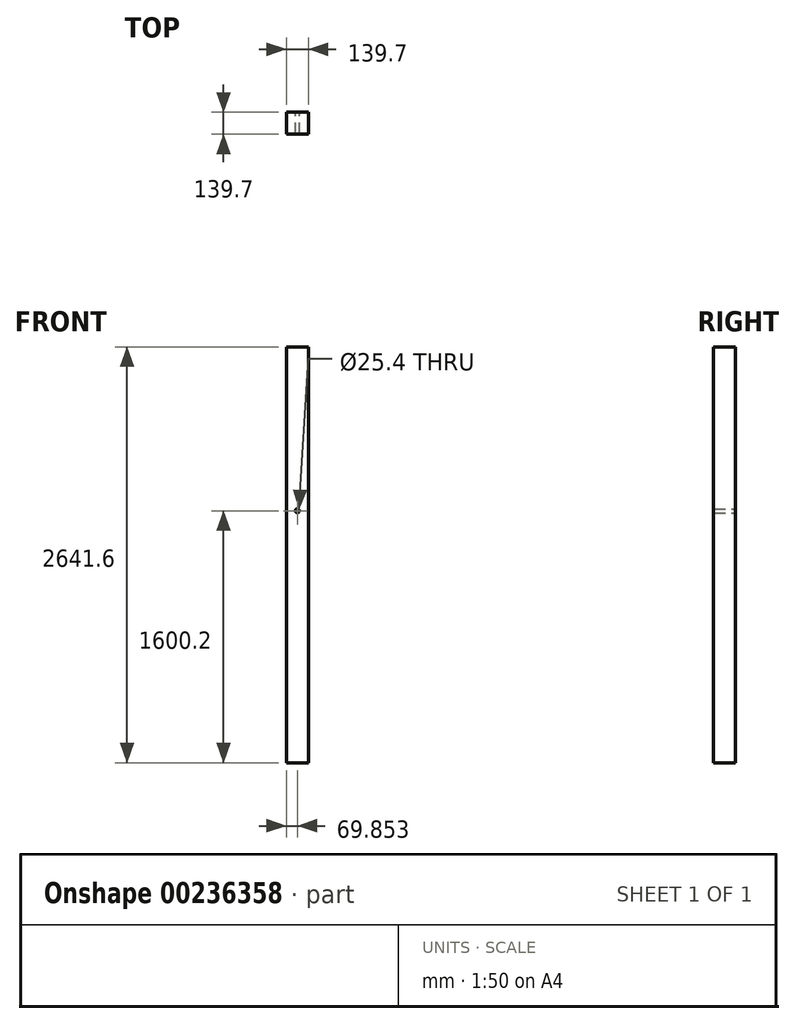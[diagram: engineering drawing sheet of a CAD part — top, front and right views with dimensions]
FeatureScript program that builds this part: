
annotation { "Feature Type Name" : "Feature", "Feature Type Description" : "" }
export const myFeature = defineFeature(function(context is Context, id is Id, definition is map)
    precondition{}
    {
        {
            var Q0;
            Q0=qCreatedBy(makeId("Front.planeOp"),FACE);
            var sketch = newSketch(context, id + "F0", { "sketchPlane" : qUnion([Q0])});
            skLineSegment(sketch, "E0.bottom", {"start": v(-1334.93, 1334.25) * mm, "end": v(-1195.23, 1334.25) * mm});
            skLineSegment(sketch, "E0.top", {"start": v(-1334.93, -1307.35) * mm, "end": v(-1195.23, -1307.35) * mm});
            skLineSegment(sketch, "E0.left", {"start": v(-1334.93, 1334.25) * mm, "end": v(-1334.93, -1307.35) * mm});
            skLineSegment(sketch, "E0.right", {"start": v(-1195.23, 1334.25) * mm, "end": v(-1195.23, -1307.35) * mm});
            skCircle(sketch, "E1", {"center": v(-1265.08, 292.85) * mm, "radius": 12.7 * mm});
            skSolve(sketch);
        }
        {
            var Q0;
            Q0=makeQuery(id+"F0.imprint","IMPRINT",FACE,{"disambiguationData":[TD([[makeQuery(id+"F0.imprint","IMPRINT",EDGE,{"derivedFrom":sQuery(id+"F0.wireOp",EDGE,"E0.bottom")}),-1.0]])]});
            extrude(context, id + "F1", {"entities" : qUnion([Q0]), "depth" : 139.7 * mm});
        }
    });
